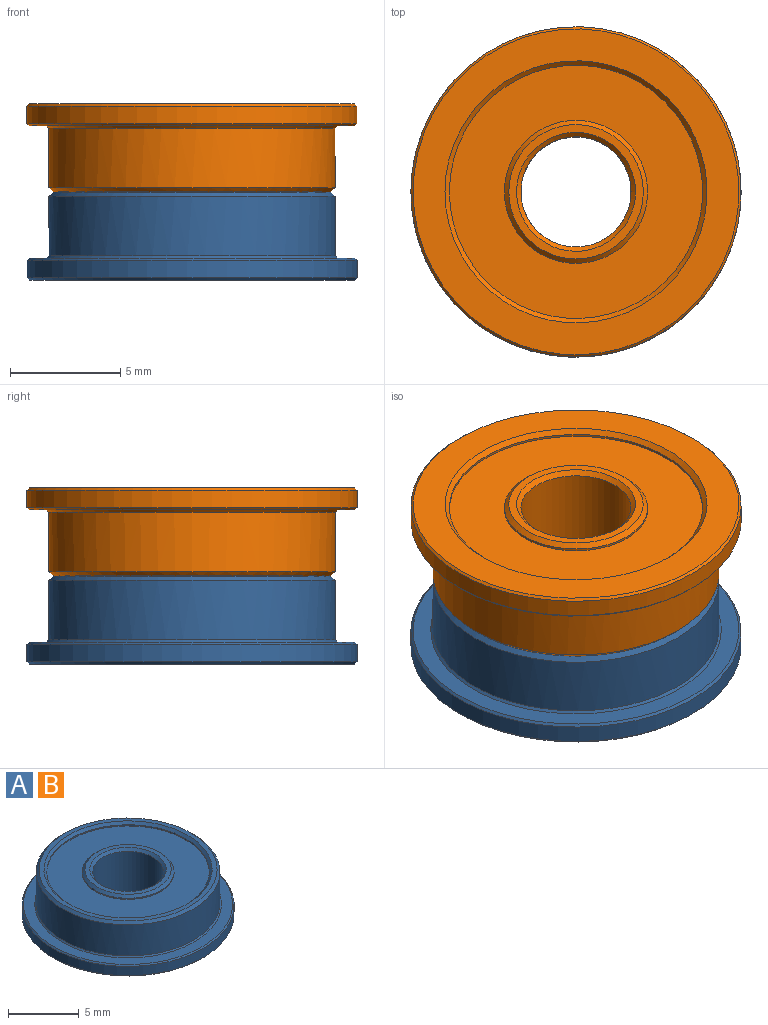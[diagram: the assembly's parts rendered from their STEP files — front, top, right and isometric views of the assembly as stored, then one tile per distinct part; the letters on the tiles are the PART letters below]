
ASSEMBLY  parts=2 mates=1
PART A: 24 faces, bbox 15x15x4 mm
  f0: cone r=6.55mm half-angle=45deg, axis (0,0,-1), area 5.8mm2, adj f1,f2
  f1: plane 14.8x14.8mm, normal (0,0,1), area 35.2mm2, adj f0,f3
  f2: cylinder r=6.5mm len=13mm, axis (0,0,1), area 110.3mm2, adj f0,f15
  f3: cone r=7.45mm half-angle=45deg, axis (0,0,-1), area 6.6mm2, adj f1,f4
  f4: cylinder r=7.5mm len=15mm, axis (0,0,1), area 37.7mm2, adj f3,f5
  f5: cone r=7.45mm half-angle=45deg, axis (0,0,1), area 6.6mm2, adj f4,f6
  f6: plane 14.8x14.8mm, normal (0,0,-1), area 60.8mm2, adj f5,f12
  f7: cone r=2.6mm half-angle=45deg, axis (0,0,-1), area 4.6mm2, adj f8,f9
  f8: plane 6.1x6.1mm, normal (0,0,-1), area 6.3mm2, adj f7,f10
  f9: cylinder r=2.5mm len=5mm, axis (0,0,-1), area 56.5mm2, adj f7,f22
  f10: cone r=3.15mm half-angle=45deg, axis (0,0,1), area 5.6mm2, adj f8,f11
  f11: cylinder r=3.25mm len=6.5mm, axis (0,0,1), area 2mm2, adj f10,f14
  f12: cone r=5.85mm half-angle=45deg, axis (0,0,-1), area 10.4mm2, adj f6,f13
  f13: cylinder r=5.75mm len=11.5mm, axis (0,0,1), area 3.6mm2, adj f12,f14
  f14: plane 11.5x11.5mm, normal (0,0,-1), area 70.7mm2, adj f11,f13
  f15: cone r=6.4mm half-angle=45deg, axis (0,0,-1), area 11.4mm2, adj f2,f16
  f16: plane 12.6x12.6mm, normal (0,0,1), area 13.5mm2, adj f15,f17
  f17: cone r=5.85mm half-angle=45deg, axis (0,0,1), area 10.4mm2, adj f16,f18
  f18: cylinder r=5.75mm len=11.5mm, axis (0,0,-1), area 3.6mm2, adj f17,f23
  f19: cone r=3.15mm half-angle=45deg, axis (0,0,-1), area 5.6mm2, adj f20,f21
  f20: plane 6.1x6.1mm, normal (0,0,1), area 6.3mm2, adj f19,f22
  f21: cylinder r=3.25mm len=6.5mm, axis (0,0,-1), area 2mm2, adj f19,f23
  f22: cone r=2.6mm half-angle=45deg, axis (0,0,1), area 4.6mm2, adj f9,f20
  f23: plane 11.5x11.5mm, normal (0,0,1), area 70.7mm2, adj f18,f21
PART B: same geometry as A
PLACE A t=(0,0,12.98)mm
PLACE B rot(axis=(0,-1,0),180deg) t=(0,0,20.98)mm
MATE fastened A.f5 <-> B.f5  axis (0,0,1) through (0,0,16.98)mm
